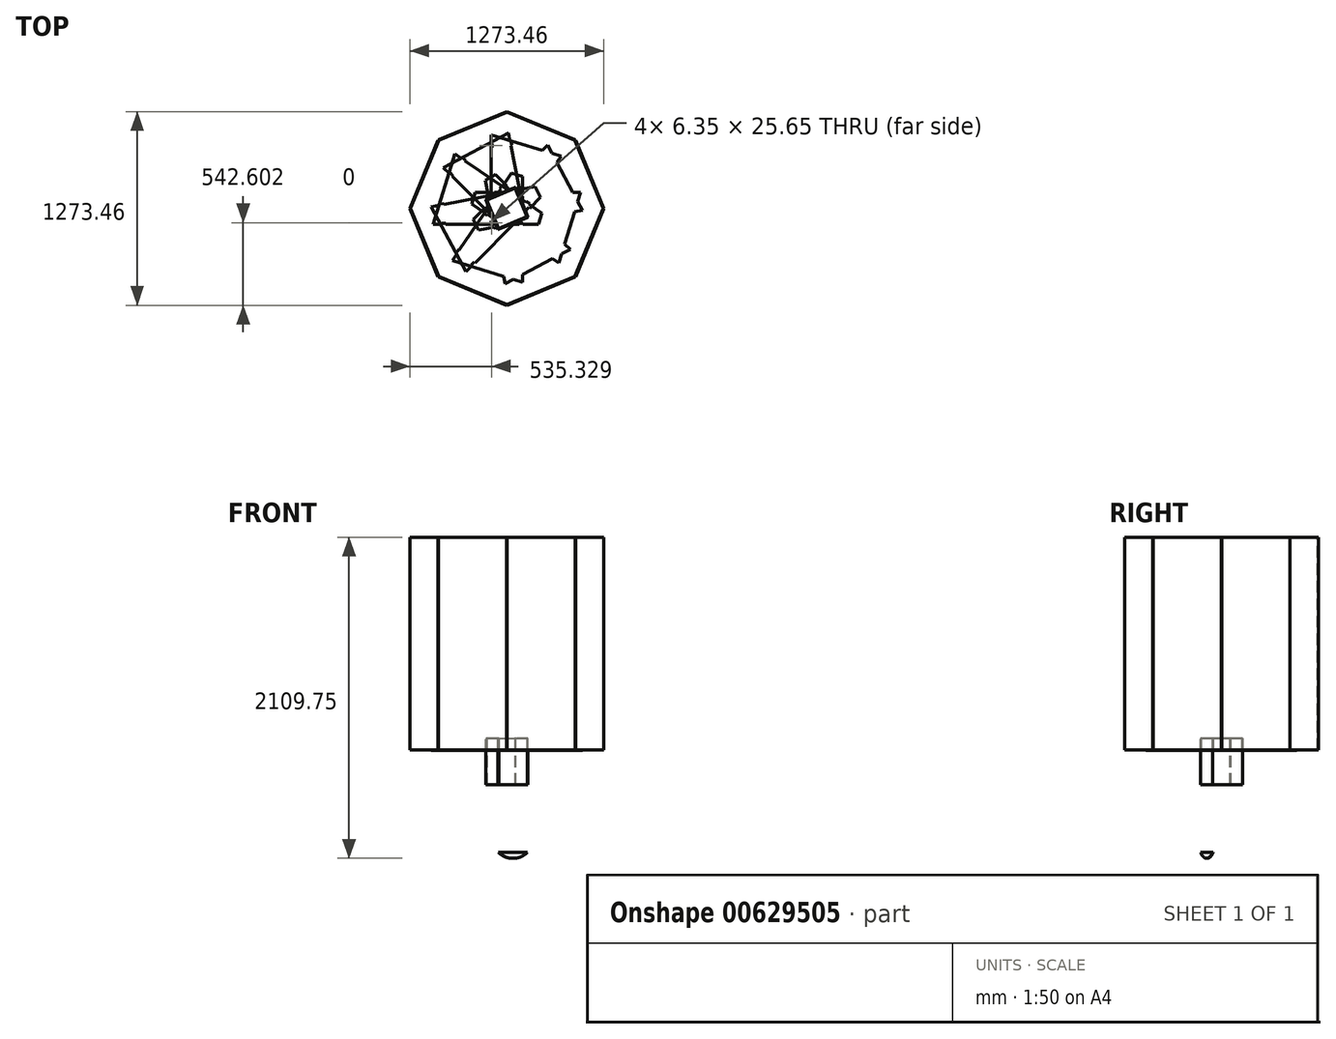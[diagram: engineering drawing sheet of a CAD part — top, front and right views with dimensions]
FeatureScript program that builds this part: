
annotation { "Feature Type Name" : "Feature", "Feature Type Description" : "" }
export const myFeature = defineFeature(function(context is Context, id is Id, definition is map)
    precondition{}
    {
        {
            var Q0;
            Q0=qCreatedBy(makeId("Top.planeOp"),FACE);
            var sketch = newSketch(context, id + "F0", { "sketchPlane" : qUnion([Q0])});
            skCircle(sketch, "E0.cCircle", {"center": v(0, 0) * mm, "radius": 584.2 * mm, "construction": true});
            skLineSegment(sketch, "E0.0", {"start": v(-632.33, 0) * mm, "end": v(-447.13, 447.13) * mm});
            skLineSegment(sketch, "E0.1", {"start": v(-447.13, 447.13) * mm, "end": v(0, 632.33) * mm});
            skLineSegment(sketch, "E0.2", {"start": v(0, 632.33) * mm, "end": v(447.13, 447.13) * mm});
            skLineSegment(sketch, "E0.3", {"start": v(447.13, 447.13) * mm, "end": v(632.33, 0) * mm});
            skLineSegment(sketch, "E0.4", {"start": v(632.33, 0) * mm, "end": v(447.13, -447.13) * mm});
            skLineSegment(sketch, "E0.5", {"start": v(447.13, -447.13) * mm, "end": v(0, -632.33) * mm});
            skLineSegment(sketch, "E0.6", {"start": v(0, -632.33) * mm, "end": v(-447.13, -447.13) * mm});
            skLineSegment(sketch, "E0.7", {"start": v(-447.13, -447.13) * mm, "end": v(-632.33, 0) * mm});
            skPoint(sketch, "E0.0.midPoint", {"position": v(0, 584.2) * mm});
            skSolve(sketch);
        }
        {
            var Q0;
            Q0=qCreatedBy(makeId("Front.planeOp"),FACE);
            var sketch = newSketch(context, id + "F1", { "sketchPlane" : qUnion([Q0])});
            skLineSegment(sketch, "E1", {"start": v(0, 0) * mm, "end": v(0, -445.34) * mm});
            skLineSegment(sketch, "E2", {"start": v(101.6, -445.34) * mm, "end": v(632.33, 0) * mm});
            skLineSegment(sketch, "E3", {"start": v(101.6, -445.34) * mm, "end": v(0, -445.34) * mm});
            skSolve(sketch);
        }
        {
            var Q0;
            Q0=qCreatedBy(makeId("Top.planeOp"),FACE);
            var Q1;
            Q1=sQuery(id+"F1.wireOp",VERTEX,"E2.end");
            cPlane(context, id + "F2", {"entities" : qUnion([Q0, Q1]), "cplaneType" : CPlaneType.PLANE_POINT, "offset" : 381 * mm, "oppositeDirection" : true, "width" : 152.4 * mm, "height" : 152.4 * mm});
        }
        {
            var Q0;
            Q0=qCreatedBy(id+"F2.planeOp",FACE);
            var sketch = newSketch(context, id + "F3", { "sketchPlane" : qUnion([Q0])});
            skCircle(sketch, "E4.cCircle", {"center": v(0, 0) * mm, "radius": 93.87 * mm, "construction": true});
            skLineSegment(sketch, "E4.0", {"start": v(-71.84, 71.84) * mm, "end": v(0, 101.6) * mm});
            skLineSegment(sketch, "E4.1", {"start": v(0, 101.6) * mm, "end": v(71.84, 71.84) * mm});
            skLineSegment(sketch, "E4.2", {"start": v(71.84, 71.84) * mm, "end": v(101.6, 0) * mm});
            skLineSegment(sketch, "E4.3", {"start": v(101.6, 0) * mm, "end": v(71.84, -71.84) * mm});
            skLineSegment(sketch, "E4.4", {"start": v(71.84, -71.84) * mm, "end": v(0, -101.6) * mm});
            skLineSegment(sketch, "E4.5", {"start": v(0, -101.6) * mm, "end": v(-71.84, -71.84) * mm});
            skLineSegment(sketch, "E4.6", {"start": v(-71.84, -71.84) * mm, "end": v(-101.6, 0) * mm});
            skLineSegment(sketch, "E4.7", {"start": v(-101.6, 0) * mm, "end": v(-71.84, 71.84) * mm});
            skSolve(sketch);
        }
        {
            var Q0;
            Q0=sQuery(id+"F3.wireOp",VERTEX,"E4.2.start");
            var Q1;
            Q1=sQuery(id+"F0.wireOp",VERTEX,"E0.1.end");
            var Q2;
            Q2=sQuery(id+"F0.wireOp",VERTEX,"E0.3.start");
            cPlane(context, id + "F4", {"entities" : qUnion([Q0, Q1, Q2]), "cplaneType" : CPlaneType.THREE_POINT, "offset" : 25.4 * mm, "width" : 152.4 * mm, "height" : 152.4 * mm});
        }
        {
            var Q0;
            Q0=qCreatedBy(id+"F4.planeOp",FACE);
            var sketch = newSketch(context, id + "F5", { "sketchPlane" : qUnion([Q0])});
            skLineSegment(sketch, "E5", {"start": v(358.13, 342.52) * mm, "end": v(-104.58, 484.4) * mm});
            skLineSegment(sketch, "E6", {"start": v(-104.58, 484.4) * mm, "end": v(-104.58, -208.43) * mm});
            skLineSegment(sketch, "E7", {"start": v(-104.58, -208.43) * mm, "end": v(-30.23, -231.22) * mm});
            skLineSegment(sketch, "E8", {"start": v(-30.23, -231.22) * mm, "end": v(358.13, 342.52) * mm});
            skSolve(sketch);
        }
        {
            var Q0;
            Q0=qSketchRegion(id+"F5",true);
            extrude(context, id + "F6", {"entities" : qUnion([Q0]), "oppositeDirection" : true, "depth" : 4.76 * mm});
        }
        {
            var Q0;
            Q0=qCreatedBy(id+"F4.planeOp",FACE);
            var sketch = newSketch(context, id + "F7", { "sketchPlane" : qUnion([Q0])});
            skLineSegment(sketch, "E9", {"start": v(-104.58, 426.57) * mm, "end": v(-98.23, 426.57) * mm});
            skLineSegment(sketch, "E10", {"start": v(-98.23, 426.57) * mm, "end": v(-98.23, 400.92) * mm});
            skLineSegment(sketch, "E11", {"start": v(-98.23, 400.92) * mm, "end": v(-104.58, 400.92) * mm});
            skLineSegment(sketch, "E12", {"start": v(-104.58, -81.3) * mm, "end": v(-98.23, -81.3) * mm});
            skLineSegment(sketch, "E13", {"start": v(-98.23, -81.3) * mm, "end": v(-98.23, -106.95) * mm});
            skLineSegment(sketch, "E14", {"start": v(-98.23, -106.95) * mm, "end": v(-104.58, -106.95) * mm});
            skLineSegment(sketch, "E15", {"start": v(-104.58, -106.95) * mm, "end": v(-104.58, -81.3) * mm});
            skLineSegment(sketch, "E16", {"start": v(-104.58, 400.92) * mm, "end": v(-104.58, 426.57) * mm});
            skSolve(sketch);
        }
        {
            var Q0;
            Q0=qSketchRegion(id+"F7",true);
            extrude(context, id + "F8", {"entities" : qUnion([Q0]), "operationType" : NewBodyOperationType.REMOVE, "endBound" : BoundingType.THROUGH_ALL, "oppositeDirection" : true, "depth" : 25.4 * mm});
        }
        {
            var Q0;
            Q0=qCreatedBy(id+"F4.planeOp",FACE);
            var sketch = newSketch(context, id + "F9", { "sketchPlane" : qUnion([Q0])});
            skLineSegment(sketch, "E17", {"start": v(26.72, -147.09) * mm, "end": v(31.98, -150.65) * mm});
            skLineSegment(sketch, "E18", {"start": v(31.98, -150.65) * mm, "end": v(46.22, -129.61) * mm});
            skLineSegment(sketch, "E19", {"start": v(46.22, -129.61) * mm, "end": v(40.96, -126.05) * mm});
            skLineSegment(sketch, "E20", {"start": v(40.96, -126.05) * mm, "end": v(26.72, -147.09) * mm});
            skLineSegment(sketch, "E21", {"start": v(311.48, 273.6) * mm, "end": v(325.72, 294.63) * mm});
            skLineSegment(sketch, "E22", {"start": v(325.72, 294.63) * mm, "end": v(330.97, 291.08) * mm});
            skLineSegment(sketch, "E23", {"start": v(330.97, 291.08) * mm, "end": v(316.74, 270.04) * mm});
            skLineSegment(sketch, "E24", {"start": v(316.74, 270.04) * mm, "end": v(311.48, 273.6) * mm});
            skSolve(sketch);
        }
        {
            var Q0;
            Q0=qSketchRegion(id+"F9",true);
            var Q1;
            Q1=makeQuery(id+"F6.opExtrude","CAP_FACE",FACE,{"disambiguationData":[OSD([sQuery(id+"F5.wireOp",EDGE,"E5"),sQuery(id+"F5.wireOp",EDGE,"E6"),sQuery(id+"F5.wireOp",EDGE,"E7"),sQuery(id+"F5.wireOp",EDGE,"E8")])],"isStart":false});
            extrude(context, id + "F10", {"entities" : qUnion([Q0]), "operationType" : NewBodyOperationType.ADD, "endBound" : BoundingType.UP_TO_SURFACE, "oppositeDirection" : true, "endBoundEntityFace" : qUnion([Q1]), "depth" : 25.4 * mm});
        }
        {
            var Q0;
            Q0=sQuery(id+"F0.wireOp",EDGE,"E0.2");
            cPlane(context, id + "F11", {"entities" : qUnion([Q0]), "cplaneType" : CPlaneType.LINE_ANGLE, "offset" : 25.4 * mm, "angle" : 0 * degree, "width" : 152.4 * mm, "height" : 152.4 * mm});
        }
        {
            var Q0;
            Q0=qCreatedBy(id+"F11.planeOp",FACE);
            var sketch = newSketch(context, id + "F12", { "sketchPlane" : qUnion([Q0])});
            skLineSegment(sketch, "E25.bottom", {"start": v(-241.98, 0) * mm, "end": v(241.98, 0) * mm});
            skLineSegment(sketch, "E25.top", {"start": v(-241.98, 1397) * mm, "end": v(241.98, 1397) * mm});
            skLineSegment(sketch, "E25.left", {"start": v(-241.98, 0) * mm, "end": v(-241.98, 1397) * mm});
            skLineSegment(sketch, "E25.right", {"start": v(241.98, 0) * mm, "end": v(241.98, 1397) * mm});
            skSolve(sketch);
        }
        {
            var Q0;
            Q0=qSketchRegion(id+"F12",true);
            extrude(context, id + "F13", {"entities" : qUnion([Q0]), "depth" : 4.76 * mm});
        }
        {
            var Q0;
            Q0=makeQuery(id+"F6.opExtrude","SWEPT_BODY",BODY,{"disambiguationData":[OSD([sQuery(id+"F5.wireOp",EDGE,"E5"),sQuery(id+"F5.wireOp",EDGE,"E6"),sQuery(id+"F5.wireOp",EDGE,"E7"),sQuery(id+"F5.wireOp",EDGE,"E8")])]});
            var Q1;
            Q1=makeQuery(id+"F13.opExtrude","SWEPT_BODY",BODY,{"disambiguationData":[OSD([sQuery(id+"F12.wireOp",EDGE,"E25.bottom"),sQuery(id+"F12.wireOp",EDGE,"E25.top"),sQuery(id+"F12.wireOp",EDGE,"E25.left"),sQuery(id+"F12.wireOp",EDGE,"E25.right")])]});
            var Q2;
            Q2=sQuery(id+"F0.wireOp",EDGE,"E0.cCircle");
            circularPattern(context, id + "F14", {"entities" : qUnion([Q0, Q1]), "axis" : qUnion([Q2]), "angle" : 360 * degree, "instanceCount" : 8, "equalSpace" : true});
        }
        {
            var Q0;
            Q0=qCreatedBy(id+"F2.planeOp",FACE);
            var sketch = newSketch(context, id + "F15", { "sketchPlane" : qUnion([Q0])});
            skLineSegment(sketch, "E26", {"start": v(-54.99, -132.75) * mm, "end": v(132.75, -54.99) * mm});
            skLineSegment(sketch, "E27", {"start": v(132.75, -54.99) * mm, "end": v(54.99, 132.75) * mm});
            skLineSegment(sketch, "E28", {"start": v(54.99, 132.75) * mm, "end": v(-132.75, 54.99) * mm});
            skLineSegment(sketch, "E29", {"start": v(-132.75, 54.99) * mm, "end": v(-54.99, -132.75) * mm});
            skLineSegment(sketch, "E30", {"start": v(-38.88, 93.87) * mm, "end": v(-223.56, 539.73) * mm, "construction": true});
            skLineSegment(sketch, "E31", {"start": v(-93.87, -38.88) * mm, "end": v(-544.13, -225.39) * mm, "construction": true});
            skLineSegment(sketch, "E32.0", {"start": v(-138.97, 57.56) * mm, "end": v(-57.56, -138.97) * mm});
            skLineSegment(sketch, "E32.1", {"start": v(57.56, 138.97) * mm, "end": v(-138.97, 57.56) * mm});
            skLineSegment(sketch, "E32.2", {"start": v(138.97, -57.56) * mm, "end": v(57.56, 138.97) * mm});
            skLineSegment(sketch, "E32.3", {"start": v(-57.56, -138.97) * mm, "end": v(138.97, -57.56) * mm});
            skLineSegment(sketch, "E33", {"start": v(-54.99, -132.75) * mm, "end": v(-53.16, -137.15) * mm});
            skLineSegment(sketch, "E34", {"start": v(132.75, -54.99) * mm, "end": v(134.57, -59.39) * mm});
            skLineSegment(sketch, "E35", {"start": v(54.99, 132.75) * mm, "end": v(53.16, 137.15) * mm});
            skLineSegment(sketch, "E36", {"start": v(-132.75, 54.99) * mm, "end": v(-134.57, 59.39) * mm});
            skSolve(sketch);
        }
        {
            var Q0;
            Q0=makeQuery(id+"F15.imprint","IMPRINT",FACE,{"disambiguationData":[TD([[makeQuery(id+"F15.imprint","IMPRINT",EDGE,{"derivedFrom":sQuery(id+"F15.wireOp",EDGE,"E26")}),1.0]])]});
            extrude(context, id + "F16", {"entities" : qUnion([Q0]), "operationType" : NewBodyOperationType.REMOVE, "endBound" : BoundingType.THROUGH_ALL, "depth" : 25.4 * mm, "hasSecondDirection" : true, "secondDirectionBound" : BoundingType.THROUGH_ALL, "secondDirectionOppositeDirection" : true, "secondDirectionDepth" : 25.4 * mm});
        }
        {
            var Q0;
            Q0=makeQuery(id+"F15.imprint","IMPRINT",FACE,{"disambiguationData":[TD([[makeQuery(id+"F15.imprint","IMPRINT",EDGE,{"derivedFrom":sQuery(id+"F15.wireOp",EDGE,"E26")}),-1.0]])]});
            extrude(context, id + "F17", {"entities" : qUnion([Q0]), "depth" : 76.2 * mm, "hasSecondDirection" : true, "secondDirectionOppositeDirection" : true, "secondDirectionDepth" : 228.6 * mm});
        }
        {
            var Q0;
            Q0=makeQuery(id+"F15.imprint","IMPRINT",FACE,{"disambiguationData":[TD([[makeQuery(id+"F15.imprint","IMPRINT",EDGE,{"derivedFrom":sQuery(id+"F15.wireOp",EDGE,"E29")}),-1.0]])]});
            var Q1;
            Q1=makeQuery(id+"F17.opExtrude","CAP_FACE",FACE,{"disambiguationData":[OSD([sQuery(id+"F15.wireOp",EDGE,"E26"),sQuery(id+"F15.wireOp",EDGE,"E32.3"),sQuery(id+"F15.wireOp",EDGE,"E33"),sQuery(id+"F15.wireOp",EDGE,"E34")])],"isStart":true});
            var Q2;
            Q2=makeQuery(id+"F17.opExtrude","CAP_FACE",FACE,{"disambiguationData":[OSD([sQuery(id+"F15.wireOp",EDGE,"E26"),sQuery(id+"F15.wireOp",EDGE,"E32.3"),sQuery(id+"F15.wireOp",EDGE,"E33"),sQuery(id+"F15.wireOp",EDGE,"E34")])],"isStart":false});
            extrude(context, id + "F18", {"entities" : qUnion([Q0]), "endBound" : BoundingType.UP_TO_SURFACE, "oppositeDirection" : true, "endBoundEntityFace" : qUnion([Q1]), "depth" : 25.4 * mm, "hasSecondDirection" : true, "secondDirectionBound" : BoundingType.UP_TO_SURFACE, "secondDirectionOppositeDirection" : false, "secondDirectionBoundEntityFace" : qUnion([Q2]), "secondDirectionDepth" : 25.4 * mm});
        }
        {
            var Q0;
            Q0=makeQuery(id+"F17.opExtrude","SWEPT_FACE",FACE,{"disambiguationData":[OSD([sQuery(id+"F15.wireOp",EDGE,"E32.3")])]});
            var sketch = newSketch(context, id + "F19", { "sketchPlane" : qUnion([Q0])});
            skLineSegment(sketch, "E37", {"start": v(-101.6, -403.47) * mm, "end": v(-44.06, -440.42) * mm, "construction": true});
            skLineSegment(sketch, "E38", {"start": v(-44.06, -440.42) * mm, "end": v(44.06, -440.42) * mm, "construction": true});
            skLineSegment(sketch, "E39", {"start": v(44.06, -440.42) * mm, "end": v(101.6, -403.47) * mm, "construction": true});
            skLineSegment(sketch, "E40.0", {"start": v(45.17, -444.23) * mm, "end": v(101.6, -408) * mm});
            skLineSegment(sketch, "E40.1", {"start": v(-45.17, -444.23) * mm, "end": v(45.17, -444.23) * mm});
            skLineSegment(sketch, "E40.2", {"start": v(-101.6, -408) * mm, "end": v(-45.17, -444.23) * mm});
            skLineSegment(sketch, "E41", {"start": v(-101.6, -369.14) * mm, "end": v(-101.6, -408) * mm});
            skLineSegment(sketch, "E42", {"start": v(-101.6, -369.14) * mm, "end": v(101.6, -369.14) * mm});
            skLineSegment(sketch, "E43", {"start": v(101.6, -369.14) * mm, "end": v(101.6, -408) * mm});
            skSolve(sketch);
        }
        {
            var Q0;
            Q0=qSketchRegion(id+"F19",true);
            extrude(context, id + "F20", {"entities" : qUnion([Q0]), "operationType" : NewBodyOperationType.REMOVE, "endBound" : BoundingType.THROUGH_ALL, "oppositeDirection" : true, "depth" : 25.4 * mm});
        }
        {
            var Q0;
            Q0=makeQuery(id+"F18.opExtrude","SWEPT_FACE",FACE,{"disambiguationData":[OSD([sQuery(id+"F15.wireOp",EDGE,"E32.0")])]});
            var sketch = newSketch(context, id + "F21", { "sketchPlane" : qUnion([Q0])});
            skLineSegment(sketch, "E44", {"start": v(-106.36, -400.4) * mm, "end": v(-44.06, -440.42) * mm, "construction": true});
            skLineSegment(sketch, "E45", {"start": v(-44.06, -440.42) * mm, "end": v(44.06, -440.42) * mm, "construction": true});
            skLineSegment(sketch, "E46", {"start": v(44.06, -440.42) * mm, "end": v(106.36, -400.4) * mm, "construction": true});
            skLineSegment(sketch, "E47.0", {"start": v(45.17, -444.23) * mm, "end": v(106.36, -404.94) * mm});
            skLineSegment(sketch, "E47.1", {"start": v(-45.17, -444.23) * mm, "end": v(45.17, -444.23) * mm});
            skLineSegment(sketch, "E47.2", {"start": v(-106.36, -404.94) * mm, "end": v(-45.17, -444.23) * mm});
            skLineSegment(sketch, "E48", {"start": v(-106.36, -404.94) * mm, "end": v(-106.36, -369.14) * mm});
            skLineSegment(sketch, "E49", {"start": v(-106.36, -369.14) * mm, "end": v(106.36, -369.14) * mm});
            skLineSegment(sketch, "E50", {"start": v(106.36, -369.14) * mm, "end": v(106.36, -404.94) * mm});
            skSolve(sketch);
        }
        {
            var Q0;
            Q0=qSketchRegion(id+"F21",true);
            extrude(context, id + "F22", {"entities" : qUnion([Q0]), "operationType" : NewBodyOperationType.REMOVE, "endBound" : BoundingType.THROUGH_ALL, "oppositeDirection" : true, "depth" : 25.4 * mm});
        }
        {
            var Q0;
            Q0=makeQuery(id+"F17.opExtrude","SWEPT_FACE",FACE,{"disambiguationData":[OSD([sQuery(id+"F15.wireOp",EDGE,"E32.3")])]});
            var sketch = newSketch(context, id + "F23", { "sketchPlane" : qUnion([Q0])});
            skLineSegment(sketch, "E51.bottom", {"start": v(-101.6, -496.14) * mm, "end": v(-106.36, -496.14) * mm});
            skLineSegment(sketch, "E51.top", {"start": v(-101.6, -508.84) * mm, "end": v(-106.36, -508.84) * mm});
            skLineSegment(sketch, "E51.left", {"start": v(-101.6, -496.14) * mm, "end": v(-101.6, -508.84) * mm});
            skLineSegment(sketch, "E51.right", {"start": v(-106.36, -496.14) * mm, "end": v(-106.36, -508.84) * mm});
            skLineSegment(sketch, "E52.bottom", {"start": v(-101.6, -623.14) * mm, "end": v(-106.36, -623.14) * mm});
            skLineSegment(sketch, "E52.top", {"start": v(-101.6, -635.84) * mm, "end": v(-106.36, -635.84) * mm});
            skLineSegment(sketch, "E52.left", {"start": v(-101.6, -623.14) * mm, "end": v(-101.6, -635.84) * mm});
            skLineSegment(sketch, "E52.right", {"start": v(-106.36, -623.14) * mm, "end": v(-106.36, -635.84) * mm});
            skSolve(sketch);
        }
        {
            var Q0;
            Q0=qSketchRegion(id+"F23",true);
            var Q1;
            Q1=makeQuery(id+"F17.opExtrude","SWEPT_FACE",FACE,{"disambiguationData":[OSD([sQuery(id+"F15.wireOp",EDGE,"E26")])]});
            extrude(context, id + "F24", {"entities" : qUnion([Q0]), "operationType" : NewBodyOperationType.ADD, "endBound" : BoundingType.UP_TO_SURFACE, "oppositeDirection" : true, "endBoundEntityFace" : qUnion([Q1]), "depth" : 25.4 * mm});
        }
        {
            var Q0;
            Q0=makeQuery(id+"F18.opExtrude","SWEPT_FACE",FACE,{"disambiguationData":[OSD([sQuery(id+"F15.wireOp",EDGE,"E32.0")])]});
            var sketch = newSketch(context, id + "F25", { "sketchPlane" : qUnion([Q0])});
            skLineSegment(sketch, "E53.0", {"start": v(101.1, -495.63) * mm, "end": v(106.36, -495.63) * mm});
            skLineSegment(sketch, "E53.1", {"start": v(101.1, -495.63) * mm, "end": v(101.1, -509.35) * mm});
            skLineSegment(sketch, "E53.2", {"start": v(101.1, -509.35) * mm, "end": v(106.36, -509.35) * mm});
            skLineSegment(sketch, "E54", {"start": v(106.36, -495.63) * mm, "end": v(106.36, -509.35) * mm});
            skLineSegment(sketch, "E55.0", {"start": v(101.1, -622.63) * mm, "end": v(106.36, -622.63) * mm});
            skLineSegment(sketch, "E55.1", {"start": v(101.1, -622.63) * mm, "end": v(101.1, -636.35) * mm});
            skLineSegment(sketch, "E55.2", {"start": v(101.1, -636.35) * mm, "end": v(106.36, -636.35) * mm});
            skLineSegment(sketch, "E56", {"start": v(106.36, -622.63) * mm, "end": v(106.36, -636.35) * mm});
            skSolve(sketch);
        }
        {
            var Q0;
            Q0=qSketchRegion(id+"F25",true);
            extrude(context, id + "F26", {"entities" : qUnion([Q0]), "operationType" : NewBodyOperationType.REMOVE, "endBound" : BoundingType.THROUGH_ALL, "oppositeDirection" : true, "depth" : 25.4 * mm});
        }
        {
            var Q0;
            {var subQ2=sQuery(id+"F23.wireOp",EDGE,"E51.top");Q0=makeQuery(id+"F24.boolean.opBoolean","SPLIT",FACE,{"disambiguationData":[TD([makeQuery(id+"F24.opExtrude","SWEPT_FACE",FACE,{"disambiguationData":[OSD([subQ2])]})])],"derivedFrom":makeQuery(id+"F17.opExtrude","SWEPT_FACE",FACE,{"disambiguationData":[OSD([sQuery(id+"F15.wireOp",EDGE,"E33")])]})});}
            var Q1;
            Q1=makeQuery(id+"F17.opExtrude","SWEPT_FACE",FACE,{"disambiguationData":[OSD([sQuery(id+"F15.wireOp",EDGE,"E34")])]});
            cPlane(context, id + "F27", {"entities" : qUnion([Q0, Q1]), "cplaneType" : CPlaneType.MID_PLANE, "offset" : 25.4 * mm, "width" : 152.4 * mm, "height" : 152.4 * mm});
        }
        {
            var Q0;
            Q0=makeQuery(id+"F24.boolean.opBoolean","MERGE",FACE,{"derivedFrom":[makeQuery(id+"F17.opExtrude","SWEPT_FACE",FACE,{"disambiguationData":[OSD([sQuery(id+"F15.wireOp",EDGE,"E32.3")])]}),makeQuery(id+"F24.opExtrude","CAP_FACE",FACE,{"disambiguationData":[OSD([sQuery(id+"F23.wireOp",EDGE,"E51.bottom"),sQuery(id+"F23.wireOp",EDGE,"E51.top"),sQuery(id+"F23.wireOp",EDGE,"E51.left"),sQuery(id+"F23.wireOp",EDGE,"E51.right")])],"isStart":true}),makeQuery(id+"F24.opExtrude","CAP_FACE",FACE,{"disambiguationData":[OSD([sQuery(id+"F23.wireOp",EDGE,"E52.bottom"),sQuery(id+"F23.wireOp",EDGE,"E52.top"),sQuery(id+"F23.wireOp",EDGE,"E52.left"),sQuery(id+"F23.wireOp",EDGE,"E52.right")])],"isStart":true})]});
            var sketch = newSketch(context, id + "F28", { "sketchPlane" : qUnion([Q0])});
            skArc(sketch, "E57", {"start": v(101.6, -673.94) * mm, "mid": v(0, -712.75) * mm, "end": v(-101.6, -673.94) * mm});
            skLineSegment(sketch, "E58", {"start": v(-101.6, -673.94) * mm, "end": v(101.6, -673.94) * mm});
            skSolve(sketch);
        }
        {
            var Q0;
            Q0=qSketchRegion(id+"F28",true);
            var Q1;
            {var subQ0=sQuery(id+"F15.wireOp",EDGE,"E26");Q1=makeQuery(id+"F24.boolean.opBoolean","MERGE",FACE,{"derivedFrom":[makeQuery(id+"F17.opExtrude","SWEPT_FACE",FACE,{"disambiguationData":[OSD([subQ0])]}),makeQuery(id+"F24.opExtrude","CAP_FACE",FACE,{"disambiguationData":[OSD([subQ0]),ownerDisambiguation([makeQuery(id+"F24.opExtrude","SWEPT_BODY",BODY,{"disambiguationData":[OSD([sQuery(id+"F23.wireOp",EDGE,"E51.bottom"),sQuery(id+"F23.wireOp",EDGE,"E51.top"),sQuery(id+"F23.wireOp",EDGE,"E51.left"),sQuery(id+"F23.wireOp",EDGE,"E51.right")])]})])],"isStart":false}),makeQuery(id+"F24.opExtrude","CAP_FACE",FACE,{"disambiguationData":[OSD([subQ0]),ownerDisambiguation([makeQuery(id+"F24.opExtrude","SWEPT_BODY",BODY,{"disambiguationData":[OSD([sQuery(id+"F23.wireOp",EDGE,"E52.bottom"),sQuery(id+"F23.wireOp",EDGE,"E52.top"),sQuery(id+"F23.wireOp",EDGE,"E52.left"),sQuery(id+"F23.wireOp",EDGE,"E52.right")])]})])],"isStart":false})]});}
            extrude(context, id + "F29", {"entities" : qUnion([Q0]), "operationType" : NewBodyOperationType.ADD, "endBound" : BoundingType.UP_TO_SURFACE, "oppositeDirection" : true, "endBoundEntityFace" : qUnion([Q1]), "depth" : 25.4 * mm});
        }
        {
            var Q0;
            Q0=makeQuery(id+"F26.boolean.opBoolean","SPLIT",FACE,{"disambiguationData":[TD([makeQuery(id+"F26.opExtrude","SWEPT_FACE",FACE,{"disambiguationData":[OSD([sQuery(id+"F25.wireOp",EDGE,"E53.2")])]})])],"derivedFrom":makeQuery(id+"F18.opExtrude","SWEPT_FACE",FACE,{"disambiguationData":[OSD([sQuery(id+"F15.wireOp",EDGE,"E32.3")])]})});
            var Q1;
            Q1=makeQuery(id+"F18.opExtrude","SWEPT_FACE",FACE,{"disambiguationData":[OSD([sQuery(id+"F15.wireOp",EDGE,"E32.1")])]});
            cPlane(context, id + "F30", {"entities" : qUnion([Q0, Q1]), "cplaneType" : CPlaneType.MID_PLANE, "offset" : 25.4 * mm, "width" : 152.4 * mm, "height" : 152.4 * mm});
        }
        {
            var Q0;
            Q0=makeQuery(id+"F17.opExtrude","SWEPT_BODY",BODY,{"disambiguationData":[OSD([sQuery(id+"F15.wireOp",EDGE,"E26"),sQuery(id+"F15.wireOp",EDGE,"E32.3"),sQuery(id+"F15.wireOp",EDGE,"E33"),sQuery(id+"F15.wireOp",EDGE,"E34")])]});
            var Q1;
            Q1=qCreatedBy(id+"F30.planeOp",FACE);
            mirror(context, id + "F31", {"entities" : qUnion([Q0]), "mirrorPlane" : qUnion([Q1])});
        }
        {
            var Q0;
            Q0=makeQuery(id+"F18.opExtrude","SWEPT_BODY",BODY,{"disambiguationData":[OSD([sQuery(id+"F15.wireOp",EDGE,"E29"),sQuery(id+"F15.wireOp",EDGE,"E32.0"),sQuery(id+"F15.wireOp",EDGE,"E32.1"),sQuery(id+"F15.wireOp",EDGE,"E32.3"),sQuery(id+"F15.wireOp",EDGE,"E33"),sQuery(id+"F15.wireOp",EDGE,"E36")])]});
            var Q1;
            Q1=qCreatedBy(id+"F27.planeOp",FACE);
            mirror(context, id + "F32", {"entities" : qUnion([Q0]), "mirrorPlane" : qUnion([Q1])});
        }
        {
            var Q0;
            {var subQ0=sQuery(id+"F5.wireOp",EDGE,"E8");var subQ1=sQuery(id+"F5.wireOp",EDGE,"E7");var subQ2=sQuery(id+"F5.wireOp",EDGE,"E6");var subQ3=sQuery(id+"F5.wireOp",EDGE,"E5");Q0=makeQuery(id+"F14.opPattern","COPY",FACE,{"derivedFrom":makeQuery(id+"F10.boolean.opBoolean","MERGE",FACE,{"derivedFrom":[makeQuery(id+"F6.opExtrude","CAP_FACE",FACE,{"disambiguationData":[OSD([subQ3,subQ2,subQ1,subQ0])],"isStart":false}),makeQuery(id+"F10.opExtrude","CAP_FACE",FACE,{"disambiguationData":[OSD([subQ3,subQ2,subQ1,subQ0]),ownerDisambiguation([makeQuery(id+"F10.opExtrude","SWEPT_BODY",BODY,{"disambiguationData":[OSD([sQuery(id+"F9.wireOp",EDGE,"E17"),sQuery(id+"F9.wireOp",EDGE,"E18"),sQuery(id+"F9.wireOp",EDGE,"E19"),sQuery(id+"F9.wireOp",EDGE,"E20")])]})])],"isStart":false}),makeQuery(id+"F10.opExtrude","CAP_FACE",FACE,{"disambiguationData":[OSD([subQ3,subQ2,subQ1,subQ0]),ownerDisambiguation([makeQuery(id+"F10.opExtrude","SWEPT_BODY",BODY,{"disambiguationData":[OSD([sQuery(id+"F9.wireOp",EDGE,"E21"),sQuery(id+"F9.wireOp",EDGE,"E22"),sQuery(id+"F9.wireOp",EDGE,"E23"),sQuery(id+"F9.wireOp",EDGE,"E24")])]})])],"isStart":false})]}),"instanceName":"7"});}
            var sketch = newSketch(context, id + "F33", { "sketchPlane" : qUnion([Q0])});
            skPoint(sketch, "E59", {"position": v(-200.65, 112.28) * mm});
            skLineSegment(sketch, "E60", {"start": v(-200.65, 112.28) * mm, "end": v(377.4, -211.17) * mm, "construction": true});
            skPoint(sketch, "E61", {"position": v(136.83, -76.57) * mm});
            skSolve(sketch);
        }
    });
